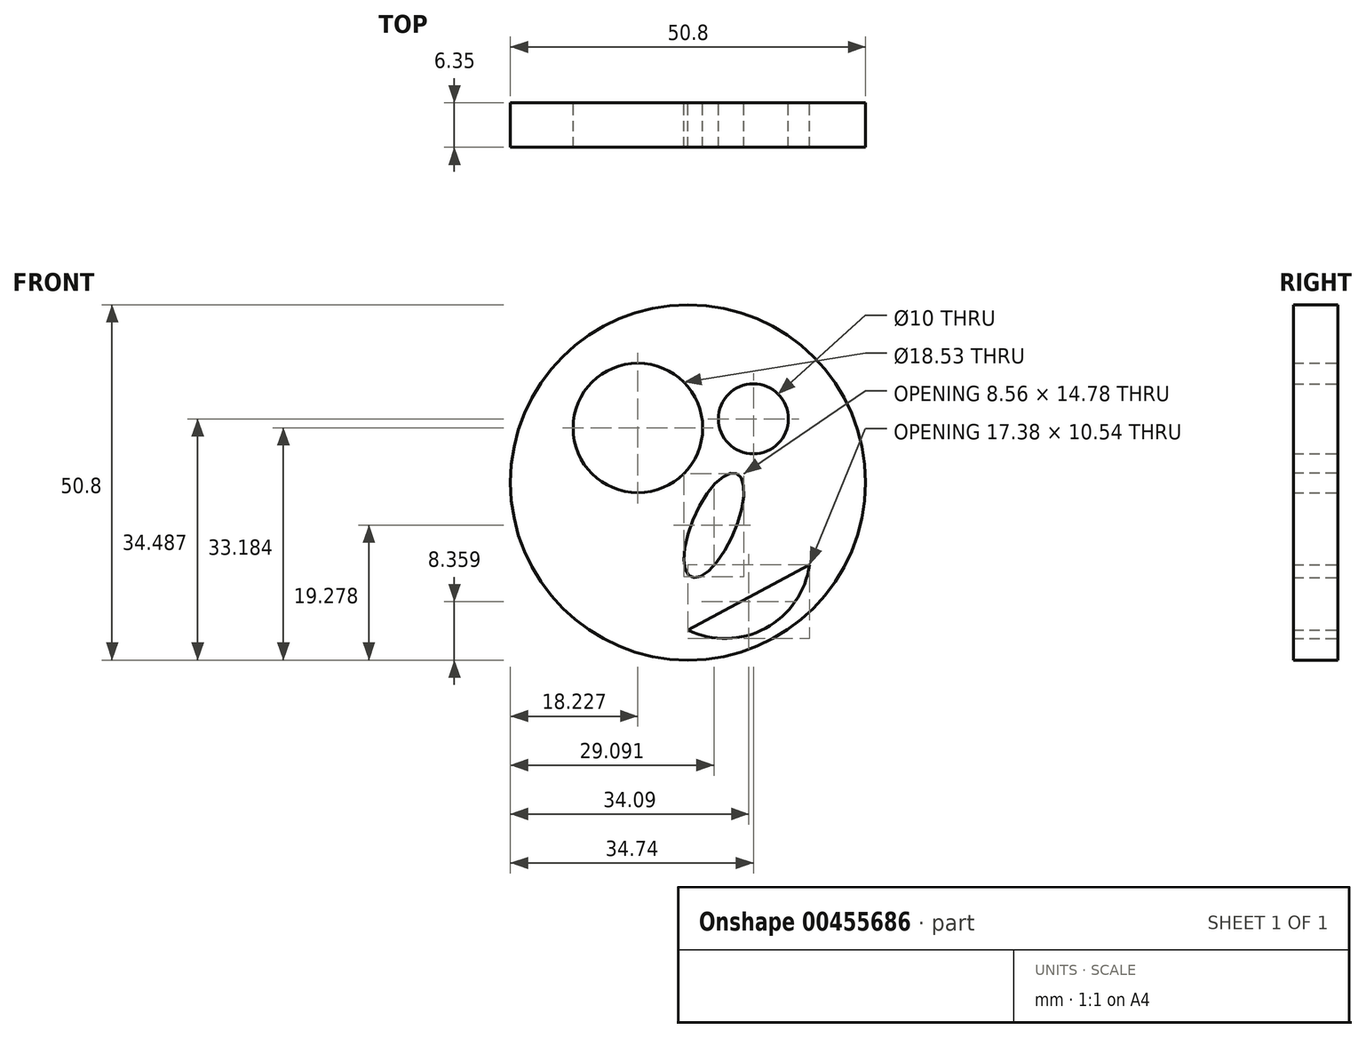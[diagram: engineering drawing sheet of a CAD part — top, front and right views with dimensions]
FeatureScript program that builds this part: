
annotation { "Feature Type Name" : "Feature", "Feature Type Description" : "" }
export const myFeature = defineFeature(function(context is Context, id is Id, definition is map)
    precondition{}
    {
        {
            var Q0;
            Q0=qCreatedBy(makeId("Front.planeOp"),FACE);
            var sketch = newSketch(context, id + "F0", { "sketchPlane" : qUnion([Q0])});
            skCircle(sketch, "E0", {"center": v(0, 0) * mm, "radius": 25.4 * mm});
            skSolve(sketch);
        }
        {
            var Q0;
            Q0 = qSketchRegion(id + "F0", true);
            extrude(context, id + "F1", {"entities" : qUnion([Q0]), "depth" : 6.35 * mm});
        }
        {
            var Q0;
            Q0=makeQuery(id+"F1.opExtrude","CAP_FACE",FACE,{"disambiguationData":[OSD([sQuery(id+"F0.wireOp",EDGE,"E0")])],"isStart":true});
            var sketch = newSketch(context, id + "F2", { "sketchPlane" : qUnion([Q0])});
            skCircle(sketch, "E1", {"center": v(-9.34, 9.09) * mm, "radius": 5 * mm});
            skCircle(sketch, "E2", {"center": v(7.17, 7.78) * mm, "radius": 9.26 * mm});
            skEllipse(sketch, "E3", {"center": v(-3.7, -6.12) * mm, "majorRadius": 8.07 * mm, "minorRadius": 3.05 * mm, "majorAxis": v(-0.4, 0.91)});
            skArc(sketch, "E4", {"start": v(-17.38, -11.77) * mm, "mid": v(-11.06, -20.86) * mm, "end": v(0, -21.11) * mm});
            skLineSegment(sketch, "E5", {"start": v(-17.38, -11.77) * mm, "end": v(0, -21.11) * mm});
            skSolve(sketch);
        }
        {
            var Q0;
            Q0 = qSketchRegion(id + "F2", true);
            extrude(context, id + "F3", {"entities" : qUnion([Q0]), "operationType" : NewBodyOperationType.REMOVE, "oppositeDirection" : true, "depth" : 304.8 * mm});
        }
    });
